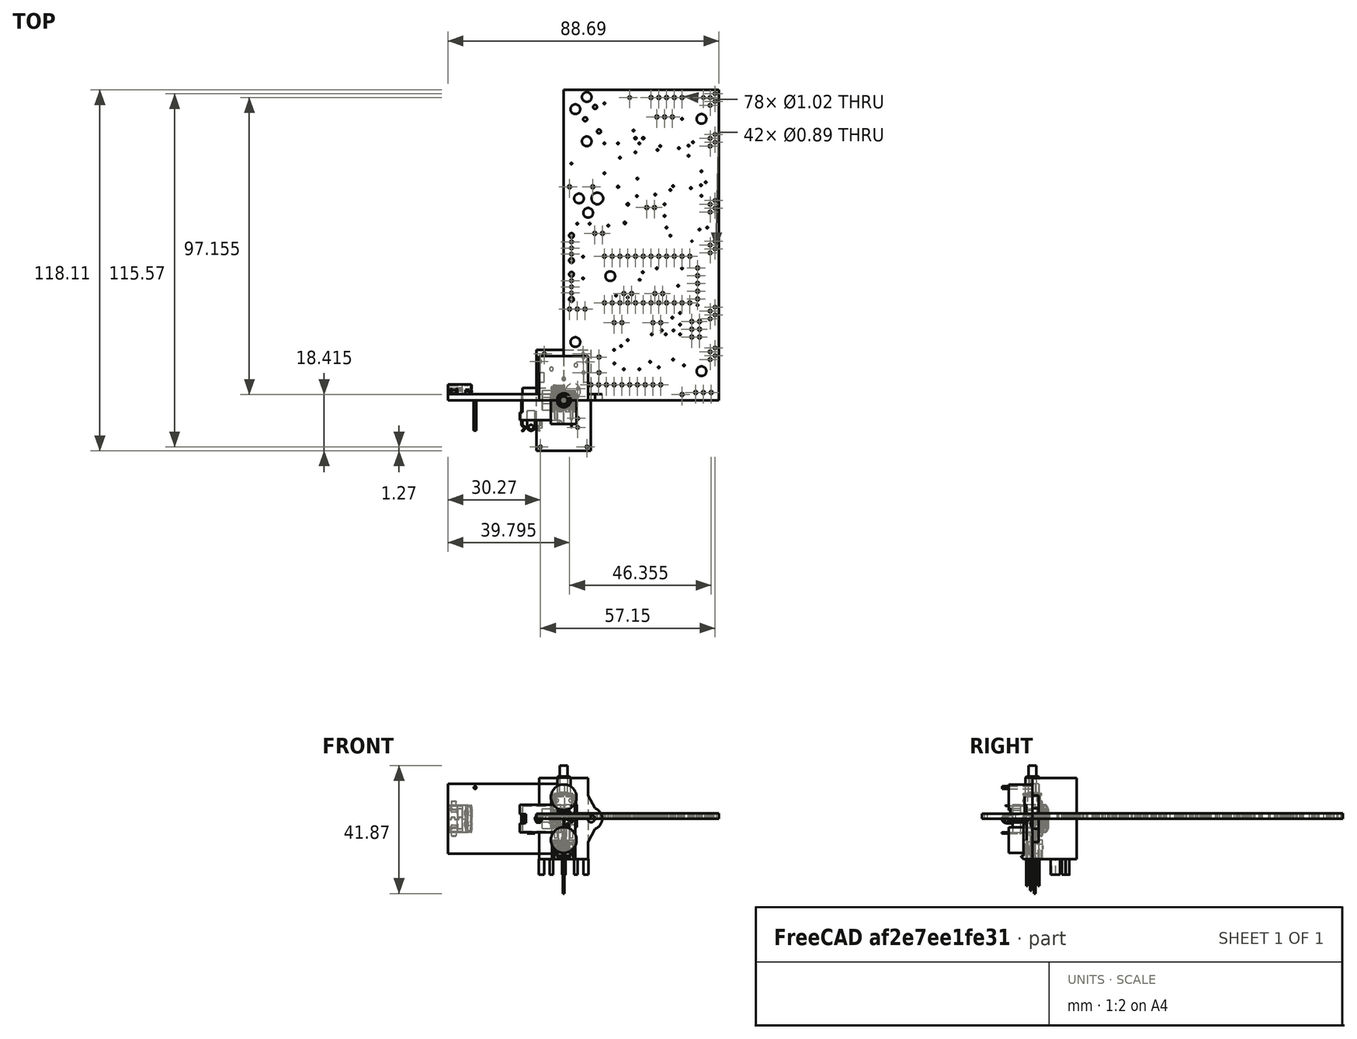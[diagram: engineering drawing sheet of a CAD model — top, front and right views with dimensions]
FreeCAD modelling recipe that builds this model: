
FCSTD DOCUMENT  (FreeCAD 1.0R39109 (Git))
Label: PCB
License: All rights reserved
LicenseURL: https://en.wikipedia.org/wiki/All_rights_reserved
objects: App::Link×17, App::FeaturePython×17, Part::Feature×15, Sketcher::SketchObject×3, App::Part×3, PartDesign::Pad×2, PartDesign::Body×2, PartDesign::Pocket×1, Assembly::JointGroup×1, Assembly::AssemblyObject×1, PartDesign::SubShapeBinder×1
note: 33 computed .brp shape members not serialized (recipe doc carries the construction recipe); baked Part::Feature solids carry a one-line shape summary decoded from their .brp

FEATURE [Sketcher::SketchObject] MainSketch
  ArcFitTolerance = 1e-06
  AttachmentSupport = -> [XY_Plane]
  FullyConstrained = false
  MakeInternals = false
  MapMode = 5
  sketch-geometry (4):
    g0: LineSegment StartX=0 StartY=0 StartZ=0 EndX=50.8 EndY=0 EndZ=0
    g1: LineSegment StartX=50.8 StartY=0 StartZ=0 EndX=50.8 EndY=101.6 EndZ=0
    g2: LineSegment StartX=50.8 StartY=101.6 StartZ=0 EndX=0 EndY=101.6 EndZ=0
    g3: LineSegment StartX=0 StartY=101.6 StartZ=0 EndX=0 EndY=0 EndZ=0
  constraints (4):
    c: Horizontal(g0)
    c: Horizontal(g2)
    c: Vertical(g1)
    c: Vertical(g3)
FEATURE [PartDesign::Pad] Main
  Direction = (0,0,1)
  Length = 1.778
  Length2 = 100.076
  Profile = -> MainSketch
  Refine = true
  Suppressed = false
  Type = 0
FEATURE [Sketcher::SketchObject] HoleSketch
  ArcFitTolerance = 1e-06
  AttachmentSupport = -> [XY_Plane]
  FullyConstrained = false
  MakeInternals = false
  MapMode = 5
  sketch-geometry (197):
    g0: Circle CenterX=41.275 CenterY=47.117 CenterZ=0 NormalX=0 NormalY=0 NormalZ=1 AngleXU=0 Radius=0.508
    g1: Circle CenterX=38.735 CenterY=47.117 CenterZ=0 NormalX=0 NormalY=0 NormalZ=1 AngleXU=0 Radius=0.508
    g2: Circle CenterX=36.195 CenterY=47.117 CenterZ=0 NormalX=0 NormalY=0 NormalZ=1 AngleXU=0 Radius=0.508
    g3: Circle CenterX=13.335 CenterY=47.117 CenterZ=0 NormalX=0 NormalY=0 NormalZ=1 AngleXU=0 Radius=0.508
    g4: Circle CenterX=33.655 CenterY=47.117 CenterZ=0 NormalX=0 NormalY=0 NormalZ=1 AngleXU=0 Radius=0.508
    g5: Circle CenterX=15.875 CenterY=47.117 CenterZ=0 NormalX=0 NormalY=0 NormalZ=1 AngleXU=0 Radius=0.508
    g6: Circle CenterX=31.115 CenterY=47.117 CenterZ=0 NormalX=0 NormalY=0 NormalZ=1 AngleXU=0 Radius=0.508
    g7: Circle CenterX=28.575 CenterY=47.117 CenterZ=0 NormalX=0 NormalY=0 NormalZ=1 AngleXU=0 Radius=0.508
    g8: Circle CenterX=26.035 CenterY=47.117 CenterZ=0 NormalX=0 NormalY=0 NormalZ=1 AngleXU=0 Radius=0.508
    g9: Circle CenterX=18.415 CenterY=47.117 CenterZ=0 NormalX=0 NormalY=0 NormalZ=1 AngleXU=0 Radius=0.508
    g10: Circle CenterX=20.955 CenterY=47.117 CenterZ=0 NormalX=0 NormalY=0 NormalZ=1 AngleXU=0 Radius=0.508
    g11: Circle CenterX=23.495 CenterY=47.117 CenterZ=0 NormalX=0 NormalY=0 NormalZ=1 AngleXU=0 Radius=0.508
    g12: Circle CenterX=15.875 CenterY=31.877 CenterZ=0 NormalX=0 NormalY=0 NormalZ=1 AngleXU=0 Radius=0.508
    g13: Circle CenterX=13.335 CenterY=31.877 CenterZ=0 NormalX=0 NormalY=0 NormalZ=1 AngleXU=0 Radius=0.508
    g14: Circle CenterX=20.955 CenterY=31.877 CenterZ=0 NormalX=0 NormalY=0 NormalZ=1 AngleXU=0 Radius=0.508
    g15: Circle CenterX=18.415 CenterY=31.877 CenterZ=0 NormalX=0 NormalY=0 NormalZ=1 AngleXU=0 Radius=0.508
    g16: Circle CenterX=26.035 CenterY=31.877 CenterZ=0 NormalX=0 NormalY=0 NormalZ=1 AngleXU=0 Radius=0.508
    g17: Circle CenterX=23.495 CenterY=31.877 CenterZ=0 NormalX=0 NormalY=0 NormalZ=1 AngleXU=0 Radius=0.508
    g18: Circle CenterX=31.115 CenterY=31.877 CenterZ=0 NormalX=0 NormalY=0 NormalZ=1 AngleXU=0 Radius=0.508
    g19: Circle CenterX=28.575 CenterY=31.877 CenterZ=0 NormalX=0 NormalY=0 NormalZ=1 AngleXU=0 Radius=0.508
    g20: Circle CenterX=36.195 CenterY=31.877 CenterZ=0 NormalX=0 NormalY=0 NormalZ=1 AngleXU=0 Radius=0.508
    g21: Circle CenterX=33.655 CenterY=31.877 CenterZ=0 NormalX=0 NormalY=0 NormalZ=1 AngleXU=0 Radius=0.508
    g22: Circle CenterX=41.275 CenterY=31.877 CenterZ=0 NormalX=0 NormalY=0 NormalZ=1 AngleXU=0 Radius=0.508
    g23: Circle CenterX=38.735 CenterY=31.877 CenterZ=0 NormalX=0 NormalY=0 NormalZ=1 AngleXU=0 Radius=0.508
    g24: Circle CenterX=22.225 CenterY=34.925 CenterZ=0 NormalX=0 NormalY=0 NormalZ=1 AngleXU=0 Radius=0.508
    g25: Circle CenterX=19.685 CenterY=34.925 CenterZ=0 NormalX=0 NormalY=0 NormalZ=1 AngleXU=0 Radius=0.508
    g26: Circle CenterX=32.385 CenterY=34.925 CenterZ=0 NormalX=0 NormalY=0 NormalZ=1 AngleXU=0 Radius=0.508
    g27: Circle CenterX=29.845 CenterY=34.925 CenterZ=0 NormalX=0 NormalY=0 NormalZ=1 AngleXU=0 Radius=0.508
    g28: Circle CenterX=43.815 CenterY=43.307 CenterZ=0 NormalX=0 NormalY=0 NormalZ=1 AngleXU=0 Radius=0.508
    g29: Circle CenterX=43.815 CenterY=40.767 CenterZ=0 NormalX=0 NormalY=0 NormalZ=1 AngleXU=0 Radius=0.508
    g30: Circle CenterX=43.815 CenterY=38.227 CenterZ=0 NormalX=0 NormalY=0 NormalZ=1 AngleXU=0 Radius=0.508
    g31: Circle CenterX=43.815 CenterY=35.687 CenterZ=0 NormalX=0 NormalY=0 NormalZ=1 AngleXU=0 Radius=0.508
    g32: Circle CenterX=43.815 CenterY=33.147 CenterZ=0 NormalX=0 NormalY=0 NormalZ=1 AngleXU=0 Radius=0.508
    g33: Circle CenterX=16.51 CenterY=25.4 CenterZ=0 NormalX=0 NormalY=0 NormalZ=1 AngleXU=0 Radius=0.508
    g34: Circle CenterX=8.89 CenterY=5.08 CenterZ=0 NormalX=0 NormalY=0 NormalZ=1 AngleXU=0 Radius=0.508
    g35: Circle CenterX=19.05 CenterY=25.4 CenterZ=0 NormalX=0 NormalY=0 NormalZ=1 AngleXU=0 Radius=0.508
    g36: Circle CenterX=11.43 CenterY=5.08 CenterZ=0 NormalX=0 NormalY=0 NormalZ=1 AngleXU=0 Radius=0.508
    g37: Circle CenterX=13.97 CenterY=5.08 CenterZ=0 NormalX=0 NormalY=0 NormalZ=1 AngleXU=0 Radius=0.508
    g38: Circle CenterX=16.51 CenterY=5.08 CenterZ=0 NormalX=0 NormalY=0 NormalZ=1 AngleXU=0 Radius=0.508
    g39: Circle CenterX=19.05 CenterY=5.08 CenterZ=0 NormalX=0 NormalY=0 NormalZ=1 AngleXU=0 Radius=0.508
    g40: Circle CenterX=21.59 CenterY=5.08 CenterZ=0 NormalX=0 NormalY=0 NormalZ=1 AngleXU=0 Radius=0.508
    g41: Circle CenterX=24.13 CenterY=5.08 CenterZ=0 NormalX=0 NormalY=0 NormalZ=1 AngleXU=0 Radius=0.508
    g42: Circle CenterX=26.67 CenterY=5.08 CenterZ=0 NormalX=0 NormalY=0 NormalZ=1 AngleXU=0 Radius=0.508
    g43: Circle CenterX=29.21 CenterY=25.4 CenterZ=0 NormalX=0 NormalY=0 NormalZ=1 AngleXU=0 Radius=0.508
    g44: Circle CenterX=29.21 CenterY=5.08 CenterZ=0 NormalX=0 NormalY=0 NormalZ=1 AngleXU=0 Radius=0.508
    g45: Circle CenterX=31.75 CenterY=25.4 CenterZ=0 NormalX=0 NormalY=0 NormalZ=1 AngleXU=0 Radius=0.508
    g46: Circle CenterX=31.75 CenterY=5.08 CenterZ=0 NormalX=0 NormalY=0 NormalZ=1 AngleXU=0 Radius=0.508
    g47: Circle CenterX=11.5358 CenterY=9.05933 CenterZ=0 NormalX=0 NormalY=0 NormalZ=1 AngleXU=0 Radius=0.508
    g48: Circle CenterX=11.5358 CenterY=14.1393 CenterZ=0 NormalX=0 NormalY=0 NormalZ=1 AngleXU=0 Radius=0.508
    g49: Circle CenterX=6.45583 CenterY=9.05933 CenterZ=0 NormalX=0 NormalY=0 NormalZ=1 AngleXU=0 Radius=0.508
    g50: Circle CenterX=6.45583 CenterY=14.1393 CenterZ=0 NormalX=0 NormalY=0 NormalZ=1 AngleXU=0 Radius=0.508
    g51: Circle CenterX=6.985 CenterY=29.845 CenterZ=0 NormalX=0 NormalY=0 NormalZ=1 AngleXU=0 Radius=0.508
    g52: Circle CenterX=4.445 CenterY=29.845 CenterZ=0 NormalX=0 NormalY=0 NormalZ=1 AngleXU=0 Radius=0.508
    g53: Circle CenterX=1.905 CenterY=29.845 CenterZ=0 NormalX=0 NormalY=0 NormalZ=1 AngleXU=0 Radius=0.508
    g54: Circle CenterX=44.45 CenterY=25.781 CenterZ=0 NormalX=0 NormalY=0 NormalZ=1 AngleXU=0 Radius=0.508
    g55: Circle CenterX=44.45 CenterY=23.241 CenterZ=0 NormalX=0 NormalY=0 NormalZ=1 AngleXU=0 Radius=0.508
    g56: Circle CenterX=44.45 CenterY=20.701 CenterZ=0 NormalX=0 NormalY=0 NormalZ=1 AngleXU=0 Radius=0.508
    g57: Circle CenterX=41.91 CenterY=25.781 CenterZ=0 NormalX=0 NormalY=0 NormalZ=1 AngleXU=0 Radius=0.508
    g58: Circle CenterX=41.91 CenterY=23.241 CenterZ=0 NormalX=0 NormalY=0 NormalZ=1 AngleXU=0 Radius=0.508
    g59: Circle CenterX=41.91 CenterY=20.701 CenterZ=0 NormalX=0 NormalY=0 NormalZ=1 AngleXU=0 Radius=0.508
    g60: Circle CenterX=43.18 CenterY=2.54 CenterZ=0 NormalX=0 NormalY=0 NormalZ=1 AngleXU=0 Radius=0.508
    g61: Circle CenterX=45.72 CenterY=2.54 CenterZ=0 NormalX=0 NormalY=0 NormalZ=1 AngleXU=0 Radius=0.508
    g62: Circle CenterX=48.26 CenterY=2.54 CenterZ=0 NormalX=0 NormalY=0 NormalZ=1 AngleXU=0 Radius=0.508
    g63: Circle CenterX=28.575 CenterY=99.06 CenterZ=0 NormalX=0 NormalY=0 NormalZ=1 AngleXU=0 Radius=0.508
    g64: Circle CenterX=31.115 CenterY=99.06 CenterZ=0 NormalX=0 NormalY=0 NormalZ=1 AngleXU=0 Radius=0.508
    g65: Circle CenterX=38.735 CenterY=99.06 CenterZ=0 NormalX=0 NormalY=0 NormalZ=1 AngleXU=0 Radius=0.508
    g66: Circle CenterX=36.195 CenterY=99.06 CenterZ=0 NormalX=0 NormalY=0 NormalZ=1 AngleXU=0 Radius=0.508
    g67: Circle CenterX=10.16 CenterY=54.61 CenterZ=0 NormalX=0 NormalY=0 NormalZ=1 AngleXU=0 Radius=0.508
    g68: Circle CenterX=12.7 CenterY=54.61 CenterZ=0 NormalX=0 NormalY=0 NormalZ=1 AngleXU=0 Radius=0.508
    g69: Circle CenterX=13.335 CenterY=97.155 CenterZ=0 NormalX=0 NormalY=0 NormalZ=1 AngleXU=0 Radius=0.254
    g70: Circle CenterX=46.5032 CenterY=71.3317 CenterZ=0 NormalX=0 NormalY=0 NormalZ=1 AngleXU=0 Radius=0.254
    g71: Circle CenterX=30.48 CenterY=92.71 CenterZ=0 NormalX=0 NormalY=0 NormalZ=1 AngleXU=0 Radius=0.508
    g72: Circle CenterX=33.02 CenterY=92.71 CenterZ=0 NormalX=0 NormalY=0 NormalZ=1 AngleXU=0 Radius=0.508
    g73: Circle CenterX=35.56 CenterY=92.71 CenterZ=0 NormalX=0 NormalY=0 NormalZ=1 AngleXU=0 Radius=0.508
    g74: Circle CenterX=45.085 CenterY=66.8867 CenterZ=0 NormalX=0 NormalY=0 NormalZ=1 AngleXU=0 Radius=0.254
    g75: Circle CenterX=25.8445 CenterY=41.91 CenterZ=0 NormalX=0 NormalY=0 NormalZ=1 AngleXU=0 Radius=0.254
    g76: Circle CenterX=44.9157 CenterY=70.4003 CenterZ=0 NormalX=0 NormalY=0 NormalZ=1 AngleXU=0 Radius=0.254
    g77: Circle CenterX=41.6348 CenterY=69.4055 CenterZ=0 NormalX=0 NormalY=0 NormalZ=1 AngleXU=0 Radius=0.254
    g78: Circle CenterX=33.655 CenterY=56.515 CenterZ=0 NormalX=0 NormalY=0 NormalZ=1 AngleXU=0 Radius=0.254
    g79: Circle CenterX=34.925 CenterY=53.8903 CenterZ=0 NormalX=0 NormalY=0 NormalZ=1 AngleXU=0 Radius=0.254
    g80: Circle CenterX=17.78 CenterY=84.074 CenterZ=0 NormalX=0 NormalY=0 NormalZ=1 AngleXU=0 Radius=0.254
    g81: Circle CenterX=38.735 CenterY=43.18 CenterZ=0 NormalX=0 NormalY=0 NormalZ=1 AngleXU=0 Radius=0.254
    g82: Circle CenterX=30.48 CenterY=43.18 CenterZ=0 NormalX=0 NormalY=0 NormalZ=1 AngleXU=0 Radius=0.254
    g83: Circle CenterX=24.8708 CenterY=39.4123 CenterZ=0 NormalX=0 NormalY=0 NormalZ=1 AngleXU=0 Radius=0.254
    g84: Circle CenterX=34.925 CenterY=68.7917 CenterZ=0 NormalX=0 NormalY=0 NormalZ=1 AngleXU=0 Radius=0.254
    g85: Circle CenterX=45.72 CenterY=99.06 CenterZ=0 NormalX=0 NormalY=0 NormalZ=1 AngleXU=0 Radius=0.4445
    g86: Circle CenterX=33.02 CenterY=60.325 CenterZ=0 NormalX=0 NormalY=0 NormalZ=1 AngleXU=0 Radius=0.254
    g87: Circle CenterX=38.735 CenterY=1.905 CenterZ=0 NormalX=0 NormalY=0 NormalZ=1 AngleXU=0 Radius=0.508
    g88: Circle CenterX=29.6968 CenterY=63.0555 CenterZ=0 NormalX=0 NormalY=0 NormalZ=1 AngleXU=0 Radius=0.508
    g89: Circle CenterX=27.1568 CenterY=63.0555 CenterZ=0 NormalX=0 NormalY=0 NormalZ=1 AngleXU=0 Radius=0.508
    g90: Circle CenterX=17.78 CenterY=69.85 CenterZ=0 NormalX=0 NormalY=0 NormalZ=1 AngleXU=0 Radius=0.3175
    g91: Circle CenterX=29.9508 CenterY=67.3312 CenterZ=0 NormalX=0 NormalY=0 NormalZ=1 AngleXU=0 Radius=0.254
    g92: Circle CenterX=23.9183 CenterY=66.8232 CenterZ=0 NormalX=0 NormalY=0 NormalZ=1 AngleXU=0 Radius=0.254
    g93: Circle CenterX=4.99533 CenterY=66.04 CenterZ=0 NormalX=0 NormalY=0 NormalZ=1 AngleXU=0 Radius=1.5875
    g94: Circle CenterX=11.0067 CenterY=66.04 CenterZ=0 NormalX=0 NormalY=0 NormalZ=1 AngleXU=0 Radius=1.905
    g95: Circle CenterX=8.001 CenterY=61.341 CenterZ=0 NormalX=0 NormalY=0 NormalZ=1 AngleXU=0 Radius=1.5875
    g96: Circle CenterX=11.5358 CenterY=87.9687 CenterZ=0 NormalX=0 NormalY=0 NormalZ=1 AngleXU=0 Radius=0.656167
    g97: Circle CenterX=10.2764 CenterY=95.9697 CenterZ=0 NormalX=0 NormalY=0 NormalZ=1 AngleXU=0 Radius=0.661458
    g98: Circle CenterX=7.02733 CenterY=91.9692 CenterZ=0 NormalX=0 NormalY=0 NormalZ=1 AngleXU=0 Radius=0.656167
    g99: Circle CenterX=7.53533 CenterY=84.7302 CenterZ=0 NormalX=0 NormalY=0 NormalZ=1 AngleXU=0 Radius=1.5875
    g100: Circle CenterX=7.53533 CenterY=99.2293 CenterZ=0 NormalX=0 NormalY=0 NormalZ=1 AngleXU=0 Radius=1.5875
    g101: Circle CenterX=13.335 CenterY=84.0528 CenterZ=0 NormalX=0 NormalY=0 NormalZ=1 AngleXU=0 Radius=0.254
    g102: Circle CenterX=33.02 CenterY=64.135 CenterZ=0 NormalX=0 NormalY=0 NormalZ=1 AngleXU=0 Radius=0.254
    g103: Circle CenterX=17.145 CenterY=34.29 CenterZ=0 NormalX=0 NormalY=0 NormalZ=1 AngleXU=0 Radius=0.254
    g104: Circle CenterX=38.1 CenterY=21.59 CenterZ=0 NormalX=0 NormalY=0 NormalZ=1 AngleXU=0 Radius=0.254
    g105: Circle CenterX=35.56 CenterY=27.0722 CenterZ=0 NormalX=0 NormalY=0 NormalZ=1 AngleXU=0 Radius=0.254
    g106: Circle CenterX=38.1 CenterY=24.765 CenterZ=0 NormalX=0 NormalY=0 NormalZ=1 AngleXU=0 Radius=0.254
    g107: Circle CenterX=38.1 CenterY=28.575 CenterZ=0 NormalX=0 NormalY=0 NormalZ=1 AngleXU=0 Radius=0.254
    g108: Circle CenterX=20.955 CenterY=33.655 CenterZ=0 NormalX=0 NormalY=0 NormalZ=1 AngleXU=0 Radius=0.254
    g109: Circle CenterX=43.815 CenterY=31.115 CenterZ=0 NormalX=0 NormalY=0 NormalZ=1 AngleXU=0 Radius=0.254
    g110: Circle CenterX=45.085 CenterY=9.525 CenterZ=0 NormalX=0 NormalY=0 NormalZ=1 AngleXU=0 Radius=1.5875
    g111: Circle CenterX=45.085 CenterY=92.075 CenterZ=0 NormalX=0 NormalY=0 NormalZ=1 AngleXU=0 Radius=1.5875
    g112: Circle CenterX=35.814 CenterY=70.0617 CenterZ=0 NormalX=0 NormalY=0 NormalZ=1 AngleXU=0 Radius=0.254
    g113: Circle CenterX=3.81 CenterY=95.25 CenterZ=0 NormalX=0 NormalY=0 NormalZ=1 AngleXU=0 Radius=1.5875
    g114: Circle CenterX=37.465 CenterY=37.465 CenterZ=0 NormalX=0 NormalY=0 NormalZ=1 AngleXU=0 Radius=0.254
    g115: Circle CenterX=21.59 CenterY=99.06 CenterZ=0 NormalX=0 NormalY=0 NormalZ=1 AngleXU=0 Radius=0.4445
    g116: Circle CenterX=35.814 CenterY=13.335 CenterZ=0 NormalX=0 NormalY=0 NormalZ=1 AngleXU=0 Radius=0.254
    g117: Circle CenterX=28.829 CenterY=21.59 CenterZ=0 NormalX=0 NormalY=0 NormalZ=1 AngleXU=0 Radius=0.254
    g118: Circle CenterX=33.401 CenterY=21.59 CenterZ=0 NormalX=0 NormalY=0 NormalZ=1 AngleXU=0 Radius=0.254
    g119: Circle CenterX=35.941 CenterY=22.86 CenterZ=0 NormalX=0 NormalY=0 NormalZ=1 AngleXU=0 Radius=0.254
    g120: Circle CenterX=32.131 CenterY=22.86 CenterZ=0 NormalX=0 NormalY=0 NormalZ=1 AngleXU=0 Radius=0.254
    g121: Circle CenterX=18.796 CenterY=17.7377 CenterZ=0 NormalX=0 NormalY=0 NormalZ=1 AngleXU=0 Radius=0.254
    g122: Circle CenterX=28.2575 CenterY=12.5942 CenterZ=0 NormalX=0 NormalY=0 NormalZ=1 AngleXU=0 Radius=0.254
    g123: Circle CenterX=20.955 CenterY=19.685 CenterZ=0 NormalX=0 NormalY=0 NormalZ=1 AngleXU=0 Radius=0.254
    g124: Circle CenterX=24.765 CenterY=10.16 CenterZ=0 NormalX=0 NormalY=0 NormalZ=1 AngleXU=0 Radius=0.254
    g125: Circle CenterX=16.5523 CenterY=12.065 CenterZ=0 NormalX=0 NormalY=0 NormalZ=1 AngleXU=0 Radius=0.254
    g126: Circle CenterX=16.4888 CenterY=16.51 CenterZ=0 NormalX=0 NormalY=0 NormalZ=1 AngleXU=0 Radius=0.254
    g127: Circle CenterX=19.685 CenterY=10.16 CenterZ=0 NormalX=0 NormalY=0 NormalZ=1 AngleXU=0 Radius=0.254
    g128: Circle CenterX=39.37 CenterY=11.43 CenterZ=0 NormalX=0 NormalY=0 NormalZ=1 AngleXU=0 Radius=0.254
    g129: Circle CenterX=33.655 CenterY=99.06 CenterZ=0 NormalX=0 NormalY=0 NormalZ=1 AngleXU=0 Radius=0.508
    g130: Circle CenterX=3.81 CenterY=19.05 CenterZ=0 NormalX=0 NormalY=0 NormalZ=1 AngleXU=0 Radius=1.5875
    g131: Circle CenterX=15.24 CenterY=40.6188 CenterZ=0 NormalX=0 NormalY=0 NormalZ=1 AngleXU=0 Radius=1.5875
    g132: Circle CenterX=42.3122 CenterY=84.455 CenterZ=0 NormalX=0 NormalY=0 NormalZ=1 AngleXU=0 Radius=0.254
    g133: Circle CenterX=40.8517 CenterY=80.01 CenterZ=0 NormalX=0 NormalY=0 NormalZ=1 AngleXU=0 Radius=0.254
    g134: Circle CenterX=40.8517 CenterY=83.3332 CenterZ=0 NormalX=0 NormalY=0 NormalZ=1 AngleXU=0 Radius=0.254
    g135: Circle CenterX=37.6767 CenterY=82.4865 CenterZ=0 NormalX=0 NormalY=0 NormalZ=1 AngleXU=0 Radius=0.254
    g136: Circle CenterX=30.6917 CenterY=81.915 CenterZ=0 NormalX=0 NormalY=0 NormalZ=1 AngleXU=0 Radius=0.254
    g137: Circle CenterX=31.5807 CenterY=83.185 CenterZ=0 NormalX=0 NormalY=0 NormalZ=1 AngleXU=0 Radius=0.254
    g138: Circle CenterX=38.735 CenterY=92.075 CenterZ=0 NormalX=0 NormalY=0 NormalZ=1 AngleXU=0 Radius=0.254
    g139: Circle CenterX=3.048 CenterY=3.048 CenterZ=0 NormalX=0 NormalY=0 NormalZ=1 AngleXU=0 Radius=2.43417
    g140: Circle CenterX=2.54 CenterY=77.47 CenterZ=0 NormalX=0 NormalY=0 NormalZ=1 AngleXU=0 Radius=0.254
    g141: Circle CenterX=26.0244 CenterY=85.7673 CenterZ=0 NormalX=0 NormalY=0 NormalZ=1 AngleXU=0 Radius=0.365125
    g142: Circle CenterX=23.4844 CenterY=85.7673 CenterZ=0 NormalX=0 NormalY=0 NormalZ=1 AngleXU=0 Radius=0.365125
    g143: Circle CenterX=24.765 CenterY=84.0317 CenterZ=0 NormalX=0 NormalY=0 NormalZ=1 AngleXU=0 Radius=0.254
    g144: Circle CenterX=18.415 CenterY=79.375 CenterZ=0 NormalX=0 NormalY=0 NormalZ=1 AngleXU=0 Radius=0.254
    g145: Circle CenterX=23.495 CenterY=81.1318 CenterZ=0 NormalX=0 NormalY=0 NormalZ=1 AngleXU=0 Radius=0.254
    g146: Circle CenterX=2.56117 CenterY=51.8372 CenterZ=0 NormalX=0 NormalY=0 NormalZ=1 AngleXU=0 Radius=0.4445
    g147: Circle CenterX=2.56117 CenterY=47.8367 CenterZ=0 NormalX=0 NormalY=0 NormalZ=1 AngleXU=0 Radius=0.4445
    g148: Circle CenterX=2.55058 CenterY=45.7306 CenterZ=0 NormalX=0 NormalY=0 NormalZ=1 AngleXU=0 Radius=0.772583
    g149: Circle CenterX=2.55058 CenterY=53.9221 CenterZ=0 NormalX=0 NormalY=0 NormalZ=1 AngleXU=0 Radius=0.772583
    g150: Circle CenterX=2.56117 CenterY=49.8263 CenterZ=0 NormalX=0 NormalY=0 NormalZ=1 AngleXU=0 Radius=0.4445
    g151: Circle CenterX=2.56117 CenterY=39.1372 CenterZ=0 NormalX=0 NormalY=0 NormalZ=1 AngleXU=0 Radius=0.4445
    g152: Circle CenterX=2.56117 CenterY=35.1367 CenterZ=0 NormalX=0 NormalY=0 NormalZ=1 AngleXU=0 Radius=0.4445
    g153: Circle CenterX=2.55058 CenterY=33.0306 CenterZ=0 NormalX=0 NormalY=0 NormalZ=1 AngleXU=0 Radius=0.772583
    g154: Circle CenterX=2.55058 CenterY=41.2327 CenterZ=0 NormalX=0 NormalY=0 NormalZ=1 AngleXU=0 Radius=0.777875
    g155: Circle CenterX=2.56117 CenterY=37.1263 CenterZ=0 NormalX=0 NormalY=0 NormalZ=1 AngleXU=0 Radius=0.4445
    g156: Circle CenterX=22.86 CenterY=88.265 CenterZ=0 NormalX=0 NormalY=0 NormalZ=1 AngleXU=0 Radius=0.254
    g157: Circle CenterX=6.35 CenterY=39.9203 CenterZ=0 NormalX=0 NormalY=0 NormalZ=1 AngleXU=0 Radius=0.254
    g158: Circle CenterX=31.115 CenterY=10.795 CenterZ=0 NormalX=0 NormalY=0 NormalZ=1 AngleXU=0 Radius=0.254
    g159: Circle CenterX=20.0025 CenterY=58.0496 CenterZ=0 NormalX=0 NormalY=0 NormalZ=1 AngleXU=0 Radius=0.365125
    g160: Circle CenterX=4.445 CenterY=57.785 CenterZ=0 NormalX=0 NormalY=0 NormalZ=1 AngleXU=0 Radius=0.254
    g161: Circle CenterX=6.35 CenterY=46.99 CenterZ=0 NormalX=0 NormalY=0 NormalZ=1 AngleXU=0 Radius=0.254
    g162: Circle CenterX=8.509 CenterY=57.8062 CenterZ=0 NormalX=0 NormalY=0 NormalZ=1 AngleXU=0 Radius=0.254
    g163: Circle CenterX=14.605 CenterY=57.15 CenterZ=0 NormalX=0 NormalY=0 NormalZ=1 AngleXU=0 Radius=0.254
    g164: Circle CenterX=24.13 CenterY=72.5593 CenterZ=0 NormalX=0 NormalY=0 NormalZ=1 AngleXU=0 Radius=0.254
    g165: Circle CenterX=13.335 CenterY=74.295 CenterZ=0 NormalX=0 NormalY=0 NormalZ=1 AngleXU=0 Radius=0.254
    g166: Circle CenterX=20.9444 CenterY=64.1244 CenterZ=0 NormalX=0 NormalY=0 NormalZ=1 AngleXU=0 Radius=0.370417
    g167: Circle CenterX=9.525 CenterY=69.85 CenterZ=0 NormalX=0 NormalY=0 NormalZ=1 AngleXU=0 Radius=0.508
    g168: Circle CenterX=1.905 CenterY=69.85 CenterZ=0 NormalX=0 NormalY=0 NormalZ=1 AngleXU=0 Radius=0.508
    g169: Circle CenterX=49.53 CenterY=100.33 CenterZ=0 NormalX=0 NormalY=0 NormalZ=1 AngleXU=0 Radius=0.4445
    g170: Circle CenterX=47.9213 CenterY=99.06 CenterZ=0 NormalX=0 NormalY=0 NormalZ=1 AngleXU=0 Radius=0.4445
    g171: Circle CenterX=49.53 CenterY=97.79 CenterZ=0 NormalX=0 NormalY=0 NormalZ=1 AngleXU=0 Radius=0.4445
    g172: Circle CenterX=47.9213 CenterY=96.52 CenterZ=0 NormalX=0 NormalY=0 NormalZ=1 AngleXU=0 Radius=0.4445
    g173: Circle CenterX=49.53 CenterY=86.995 CenterZ=0 NormalX=0 NormalY=0 NormalZ=1 AngleXU=0 Radius=0.4445
    g174: Circle CenterX=47.9213 CenterY=85.725 CenterZ=0 NormalX=0 NormalY=0 NormalZ=1 AngleXU=0 Radius=0.4445
    g175: Circle CenterX=49.53 CenterY=84.455 CenterZ=0 NormalX=0 NormalY=0 NormalZ=1 AngleXU=0 Radius=0.4445
    g176: Circle CenterX=47.9213 CenterY=83.185 CenterZ=0 NormalX=0 NormalY=0 NormalZ=1 AngleXU=0 Radius=0.4445
    g177: Circle CenterX=49.53 CenterY=65.405 CenterZ=0 NormalX=0 NormalY=0 NormalZ=1 AngleXU=0 Radius=0.4445
    g178: Circle CenterX=47.9213 CenterY=64.135 CenterZ=0 NormalX=0 NormalY=0 NormalZ=1 AngleXU=0 Radius=0.4445
    g179: Circle CenterX=49.53 CenterY=62.865 CenterZ=0 NormalX=0 NormalY=0 NormalZ=1 AngleXU=0 Radius=0.4445
    g180: Circle CenterX=47.9213 CenterY=61.595 CenterZ=0 NormalX=0 NormalY=0 NormalZ=1 AngleXU=0 Radius=0.4445
    g181: Circle CenterX=49.53 CenterY=52.07 CenterZ=0 NormalX=0 NormalY=0 NormalZ=1 AngleXU=0 Radius=0.4445
    g182: Circle CenterX=47.9213 CenterY=50.8 CenterZ=0 NormalX=0 NormalY=0 NormalZ=1 AngleXU=0 Radius=0.4445
    g183: Circle CenterX=49.53 CenterY=49.53 CenterZ=0 NormalX=0 NormalY=0 NormalZ=1 AngleXU=0 Radius=0.4445
    g184: Circle CenterX=47.9213 CenterY=48.26 CenterZ=0 NormalX=0 NormalY=0 NormalZ=1 AngleXU=0 Radius=0.4445
    g185: Circle CenterX=49.53 CenterY=30.48 CenterZ=0 NormalX=0 NormalY=0 NormalZ=1 AngleXU=0 Radius=0.4445
    g186: Circle CenterX=47.9213 CenterY=29.21 CenterZ=0 NormalX=0 NormalY=0 NormalZ=1 AngleXU=0 Radius=0.4445
    g187: Circle CenterX=49.53 CenterY=27.94 CenterZ=0 NormalX=0 NormalY=0 NormalZ=1 AngleXU=0 Radius=0.4445
    g188: Circle CenterX=47.9213 CenterY=26.67 CenterZ=0 NormalX=0 NormalY=0 NormalZ=1 AngleXU=0 Radius=0.4445
    g189: Circle CenterX=49.53 CenterY=17.145 CenterZ=0 NormalX=0 NormalY=0 NormalZ=1 AngleXU=0 Radius=0.4445
    g190: Circle CenterX=47.9213 CenterY=15.875 CenterZ=0 NormalX=0 NormalY=0 NormalZ=1 AngleXU=0 Radius=0.4445
    g191: Circle CenterX=49.53 CenterY=14.605 CenterZ=0 NormalX=0 NormalY=0 NormalZ=1 AngleXU=0 Radius=0.4445
    g192: Circle CenterX=47.9213 CenterY=13.335 CenterZ=0 NormalX=0 NormalY=0 NormalZ=1 AngleXU=0 Radius=0.4445
    g193: Circle CenterX=45.085 CenterY=74.93 CenterZ=0 NormalX=0 NormalY=0 NormalZ=1 AngleXU=0 Radius=0.254
    g194: Circle CenterX=46.99 CenterY=56.515 CenterZ=0 NormalX=0 NormalY=0 NormalZ=1 AngleXU=0 Radius=0.254
    g195: Circle CenterX=44.45 CenterY=55.88 CenterZ=0 NormalX=0 NormalY=0 NormalZ=1 AngleXU=0 Radius=0.254
    g196: Circle CenterX=41.9206 CenterY=52.07 CenterZ=0 NormalX=0 NormalY=0 NormalZ=1 AngleXU=0 Radius=0.174625
FEATURE [PartDesign::Pocket] Holes
  BaseFeature = -> Main
  Direction = (0,0,-1)
  Length = 3.556
  Length2 = 5
  Profile = -> HoleSketch
  Refine = true
  Reversed = true
  Suppressed = false
  Type = 0
FEATURE [PartDesign::Body] Body  label="pcb imported"
  AllowCompound = false
  Group = -> [MainSketch,Main,HoleSketch,Holes]
  Origin = -> Origin
  Tip = -> Holes
FEATURE [App::Link] pcb_imported  label="pcb imported001"
  LinkedObject = -> Body
FEATURE [App::FeaturePython] GroundedJoint  # Assembly grounded joint (typed FeaturePython)
  ObjectToGround = -> pcb_imported
FEATURE [Part::Feature] Part__Feature  label="WP154A4SUREQBFZGC"
  shape: bbox 5.9 x 5.487 x 33.1 mm, 95 faces (baked)
FEATURE [App::Link] WP154A4SUREQBFZGC  label="WP154A4SUREQBFZGC001"
  LinkPlacement = pos=(54.356,15.113,4.572) rot=(0,1,0;1.5708rad)
  LinkedObject = -> Part__Feature
  Placement = pos=(54.356,15.113,4.572) rot=(0,1,0;1.5708rad)
FEATURE [App::FeaturePython] Joint  label="Fixed"  # Assembly joint (typed FeaturePython)
  Activated = true
  AngleMax = 0
  AngleMin = 0
  Detach1 = false
  Detach2 = false
  Distance = 0
  Distance2 = 0
  EnableAngleMax = false
  EnableAngleMin = false
  EnableLengthMax = false
  EnableLengthMin = false
  JointType = 0 (Fixed)
  LengthMax = 0
  LengthMin = 0
  Offset1 = pos=(4.572,-15.113,-54.356) rot=(0.707107,0,0.707107;3.14159rad)
  Placement1 = pos=(4.572,-15.113,-54.356) rot=(0.707107,0,0.707107;3.14159rad)
  Reference1 = -> Assembly [WP154A4SUREQBFZGC.,WP154A4SUREQBFZGC.]
  Reference2 = -> Assembly [pcb_imported.,pcb_imported.]
FEATURE [App::Link] WP154A4SUREQBFZGC001  label="WP154A4SUREQBFZGC002"
  LinkPlacement = pos=(54.356,28.448,4.572) rot=(0,1,0;1.5708rad)
  LinkedObject = -> Part__Feature
  Placement = pos=(54.356,28.448,4.572) rot=(0,1,0;1.5708rad)
FEATURE [App::FeaturePython] Joint001  label="Fixed001"  # Assembly joint (typed FeaturePython)
  Activated = true
  AngleMax = 0
  AngleMin = 0
  Detach1 = false
  Detach2 = false
  Distance = 0
  Distance2 = 0
  EnableAngleMax = false
  EnableAngleMin = false
  EnableLengthMax = false
  EnableLengthMin = false
  JointType = 0 (Fixed)
  LengthMax = 0
  LengthMin = 0
  Offset1 = pos=(0,-13.335,0) rot=(1,0,0;3.14159rad)
  Placement1 = pos=(0,-13.335,0) rot=(1,0,0;3.14159rad)
  Reference1 = -> Assembly [WP154A4SUREQBFZGC001.,WP154A4SUREQBFZGC001.]
  Reference2 = -> Assembly [WP154A4SUREQBFZGC.,WP154A4SUREQBFZGC.]
FEATURE [App::Link] WP154A4SUREQBFZGC002  label="WP154A4SUREQBFZGC003"
  LinkPlacement = pos=(54.356,50.038,4.572) rot=(0,1,0;1.5708rad)
  LinkedObject = -> Part__Feature
  Placement = pos=(54.356,50.038,4.572) rot=(0,1,0;1.5708rad)
FEATURE [App::FeaturePython] Joint002  label="Fixed002"  # Assembly joint (typed FeaturePython)
  Activated = true
  AngleMax = 0
  AngleMin = 0
  Detach1 = false
  Detach2 = false
  Distance = 0
  Distance2 = 0
  EnableAngleMax = false
  EnableAngleMin = false
  EnableLengthMax = false
  EnableLengthMin = false
  JointType = 0 (Fixed)
  LengthMax = 0
  LengthMin = 0
  Offset1 = pos=(0,-34.925,0) rot=(0,0,1;0rad)
  Placement1 = pos=(0,-34.925,0) rot=(0,0,1;0rad)
  Reference1 = -> Assembly [WP154A4SUREQBFZGC002.,WP154A4SUREQBFZGC002.]
  Reference2 = -> Assembly [WP154A4SUREQBFZGC.,WP154A4SUREQBFZGC.]
FEATURE [App::Link] WP154A4SUREQBFZGC003  label="WP154A4SUREQBFZGC004"
  LinkPlacement = pos=(54.356,63.373,4.572) rot=(0,1,0;1.5708rad)
  LinkedObject = -> Part__Feature
  Placement = pos=(54.356,63.373,4.572) rot=(0,1,0;1.5708rad)
FEATURE [App::FeaturePython] Joint003  label="Fixed003"  # Assembly joint (typed FeaturePython)
  Activated = true
  AngleMax = 0
  AngleMin = 0
  Detach1 = false
  Detach2 = false
  Distance = 0
  Distance2 = 0
  EnableAngleMax = false
  EnableAngleMin = false
  EnableLengthMax = false
  EnableLengthMin = false
  JointType = 0 (Fixed)
  LengthMax = 0
  LengthMin = 0
  Offset1 = pos=(0,-13.335,0) rot=(0,0,1;0rad)
  Placement1 = pos=(0,-13.335,0) rot=(0,0,1;0rad)
  Reference1 = -> Assembly [WP154A4SUREQBFZGC003.,WP154A4SUREQBFZGC003.]
  Reference2 = -> Assembly [WP154A4SUREQBFZGC002.,WP154A4SUREQBFZGC002.]
FEATURE [App::Link] WP154A4SUREQBFZGC004  label="WP154A4SUREQBFZGC005"
  LinkPlacement = pos=(54.356,84.963,4.572) rot=(0,1,0;1.5708rad)
  LinkedObject = -> Part__Feature
  Placement = pos=(54.356,84.963,4.572) rot=(0,1,0;1.5708rad)
FEATURE [App::FeaturePython] Joint004  label="Fixed004"  # Assembly joint (typed FeaturePython)
  Activated = true
  AngleMax = 0
  AngleMin = 0
  Detach1 = false
  Detach2 = false
  Distance = 0
  Distance2 = 0
  EnableAngleMax = false
  EnableAngleMin = false
  EnableLengthMax = false
  EnableLengthMin = false
  JointType = 0 (Fixed)
  LengthMax = 0
  LengthMin = 0
  Offset1 = pos=(0,34.925,0) rot=(0,0,1;0rad)
  Placement1 = pos=(0,34.925,0) rot=(0,0,1;0rad)
  Reference1 = -> Assembly [WP154A4SUREQBFZGC002.,WP154A4SUREQBFZGC002.]
  Reference2 = -> Assembly [WP154A4SUREQBFZGC004.,WP154A4SUREQBFZGC004.]
FEATURE [App::Link] WP154A4SUREQBFZGC005  label="WP154A4SUREQBFZGC006"
  LinkPlacement = pos=(54.356,98.298,4.572) rot=(0,1,0;1.5708rad)
  LinkedObject = -> Part__Feature
  Placement = pos=(54.356,98.298,4.572) rot=(0,1,0;1.5708rad)
FEATURE [App::FeaturePython] Joint005  label="Fixed005"  # Assembly joint (typed FeaturePython)
  Activated = true
  AngleMax = 0
  AngleMin = 0
  Detach1 = false
  Detach2 = false
  Distance = 0
  Distance2 = 0
  EnableAngleMax = false
  EnableAngleMin = false
  EnableLengthMax = false
  EnableLengthMin = false
  JointType = 0 (Fixed)
  LengthMax = 0
  LengthMin = 0
  Offset1 = pos=(0,-13.335,0) rot=(0,0,1;0rad)
  Placement1 = pos=(0,-13.335,0) rot=(0,0,1;0rad)
  Reference1 = -> Assembly [WP154A4SUREQBFZGC005.,WP154A4SUREQBFZGC005.]
  Reference2 = -> Assembly [WP154A4SUREQBFZGC004.,WP154A4SUREQBFZGC004.]
FEATURE [Part::Feature] Part__Feature003  label="Dual RCA"
  shape: bbox 20.7 x 22.3 x 31.6 mm, 33 faces (baked)
FEATURE [App::Link] Dual_RCA  label="Dual RCA001"
  LinkPlacement = pos=(0.032625,91.9586,15.028) rot=(0,0,-1;1.5708rad)
  LinkedObject = -> Part__Feature003
  Placement = pos=(0.032625,91.9586,15.028) rot=(0,0,-1;1.5708rad)
FEATURE [App::FeaturePython] Joint008  label="Fixed008"  # Assembly joint (typed FeaturePython)
  Activated = true
  AngleMax = 0
  AngleMin = 0
  Detach1 = false
  Detach2 = false
  Distance = 0
  Distance2 = 0
  EnableAngleMax = false
  EnableAngleMin = false
  EnableLengthMax = false
  EnableLengthMin = false
  JointType = 0 (Fixed)
  LengthMax = 0
  LengthMin = 0
  Offset1 = pos=(-13.335,33.909,0) rot=(0,0,1;1.5708rad)
  Placement1 = pos=(7.03262,91.9586,1.778) rot=(0,0,1;1.5708rad)
  Placement2 = pos=(-1.42e-14,7,-13.25) rot=(0,1,0;3.14159rad)
  Reference1 = -> Assembly [pcb_imported.Face5,pcb_imported.Vertex332]
  Reference2 = -> Assembly [Dual_RCA.Face1,Dual_RCA.Edge1]
FEATURE [Part::Feature] Part__Feature004  label="Pro Mini"
  shape: bbox 17.78 x 33.02 x 1.588 mm, 16 faces (baked)
FEATURE [App::Link] Pro_Mini  label="Pro Mini001"
  LinkPlacement = pos=(28.575,39.37,11.938) rot=(0,0,1;4.71239rad)
  LinkedObject = -> Part__Feature004
  Placement = pos=(28.575,39.37,11.938) rot=(0,0,1;4.71239rad)
FEATURE [App::FeaturePython] Joint009  label="Fixed009"  # Assembly joint (typed FeaturePython)
  Activated = true
  AngleMax = 0
  AngleMin = 0
  Detach1 = false
  Detach2 = false
  Distance = 0
  Distance2 = 0
  EnableAngleMax = false
  EnableAngleMin = false
  EnableLengthMax = false
  EnableLengthMin = false
  JointType = 0 (Fixed)
  LengthMax = 0
  LengthMin = 0
  Offset1 = pos=(39.37,-28.575,-11.938) rot=(0,0,1;1.5708rad)
  Placement1 = pos=(39.37,-28.575,-11.938) rot=(0,0,1;1.5708rad)
  Reference1 = -> Assembly [Pro_Mini.,Pro_Mini.]
  Reference2 = -> Assembly [pcb_imported.,pcb_imported.]
FEATURE [Part::Feature] Part__Feature005  label="Body1"
  shape: bbox 8.13 x 5.08 x 8.03 mm, 51 faces (baked)
FEATURE [Part::Feature] Part__Feature006  label="Body2"
  shape: bbox 8.13 x 5.08 x 6.63 mm, 28 faces (baked)
FEATURE [Part::Feature] Part__Feature007  label="Body3"
  shape: bbox 8.13 x 8.61 x 1.39 mm, 44 faces (baked)
FEATURE [Part::Feature] Part__Feature008  label="Body4"
  shape: bbox 6.101 x 6.101 x 6.101 mm, 9 faces (baked)
FEATURE [Part::Feature] Part__Feature009  label="Body5"
  shape: bbox 8 x 11.33 x 3.705 mm, 42 faces (baked)
FEATURE [Part::Feature] Part__Feature010  label="Body6"
  shape: bbox 2.54 x 2.54 x 6 mm, 3 faces (baked)
FEATURE [App::Part] _00SP9B6M6RE__3DModel_STEP_520916  label="800SP9B6M6RE--3DModel-STEP-520916"
  Group = -> [Part__Feature005,Part__Feature006,Part__Feature007,Part__Feature008,Part__Feature009,Part__Feature010]
  Origin = -> Origin002
  Placement = pos=(0,3.05,-1.7005) rot=(0,0,1;0rad)
FEATURE [App::Part] SPST_momentary  label="SPST-momentary"
  Group = -> [_00SP9B6M6RE__3DModel_STEP_520916]
  Origin = -> Origin003
FEATURE [App::Link] SPST_momentary001  label="SPST-momentary001"
  LinkPlacement = pos=(9.02102,11.6417,1.678) rot=(-0.57735,0.57735,0.57735;4.18879rad)
  LinkedObject = -> SPST_momentary
  Placement = pos=(9.02102,11.6417,1.678) rot=(-0.57735,0.57735,0.57735;4.18879rad)
FEATURE [App::FeaturePython] Joint010  label="Fixed010"  # Assembly joint (typed FeaturePython)
  Activated = true
  AngleMax = 0
  AngleMin = 0
  Detach1 = false
  Detach2 = false
  Distance = 0
  Distance2 = 0
  EnableAngleMax = false
  EnableAngleMin = false
  EnableLengthMax = false
  EnableLengthMin = false
  JointType = 0 (Fixed)
  LengthMax = 0
  LengthMin = 0
  Offset1 = pos=(-14.224,-6.096,0) rot=(0,0,1;3.14159rad)
  Placement1 = pos=(4.826,11.6417,1.778) rot=(0,0,1;3.14159rad)
  Placement2 = pos=(2e-16,-2.95,5.89552) rot=(0.57735,0.57735,0.57735;4.18879rad)
  Reference1 = -> Assembly [pcb_imported.Face5,pcb_imported.Vertex223]
  Reference2 = -> Assembly [SPST_momentary001._00SP9B6M6RE__3DModel_STEP_520916.Part__Feature009.Face24,SPST_momentary001._00SP9B6M6RE__3DModel_STEP_520916.Part__Feature009.Face24]
FEATURE [Part::Feature] Part__Feature011  label="3pinconnector-640441-3"
  shape: bbox 7.62 x 7.087 x 13.21 mm, 307 faces (baked)
FEATURE [App::Link] _pinconnector_640441_3  label="3pinconnector-640441-004"
  LinkPlacement = pos=(45.7412,2.54,1.778) rot=(0,1,0;3.14159rad)
  LinkedObject = -> Part__Feature011
  Placement = pos=(45.7412,2.54,1.778) rot=(0,1,0;3.14159rad)
FEATURE [App::FeaturePython] Joint011  label="Fixed011"  # Assembly joint (typed FeaturePython)
  Activated = true
  AngleMax = 0
  AngleMin = 0
  Detach1 = false
  Detach2 = false
  Distance = 0
  Distance2 = 0
  EnableAngleMax = false
  EnableAngleMin = false
  EnableLengthMax = false
  EnableLengthMin = false
  JointType = 0 (Fixed)
  LengthMax = 0
  LengthMin = 0
  Offset1 = pos=(41.148,1.27,0) rot=(0,0,1;3.14159rad)
  Placement1 = pos=(40.259,0.508,2e-16) rot=(0,0,1;3.14159rad)
  Placement2 = pos=(5.48217,3.048,1.778) rot=(0,0,1;0rad)
  Reference1 = -> Assembly [_pinconnector_640441_3.Face186,_pinconnector_640441_3.Vertex340]
  Reference2 = -> Assembly [pcb_imported.Face5,pcb_imported.Vertex206]
FEATURE [App::Link] _pinconnector_640441_004  label="3pinconnector-640441-005"
  LinkPlacement = pos=(4.445,29.845,1.778) rot=(0,1,0;3.14159rad)
  LinkedObject = -> Part__Feature011
  Placement = pos=(4.445,29.845,1.778) rot=(0,1,0;3.14159rad)
FEATURE [App::FeaturePython] Joint012  label="Fixed012"  # Assembly joint (typed FeaturePython)
  Activated = true
  AngleMax = 0
  AngleMin = 0
  Detach1 = false
  Detach2 = false
  Distance = 0
  Distance2 = 0
  EnableAngleMax = false
  EnableAngleMin = false
  EnableLengthMax = false
  EnableLengthMin = false
  JointType = 0 (Fixed)
  LengthMax = 0
  LengthMin = 0
  Offset1 = pos=(-23.749,-2.794,0) rot=(0,0,1;3.14159rad)
  Placement1 = pos=(2.794,29.083,1.778) rot=(0,0,1;3.14159rad)
  Placement2 = pos=(1.651,-0.762,2e-16) rot=(0,0,1;0rad)
  Reference1 = -> Assembly [pcb_imported.Face5,pcb_imported.Vertex284]
  Reference2 = -> Assembly [_pinconnector_640441_004.Face186,_pinconnector_640441_004.Vertex328]
FEATURE [App::Link] _pinconnector_640441_005  label="3pinconnector-640441-006"
  LinkPlacement = pos=(33.0962,92.7862,1.778) rot=(0,1,0;3.14159rad)
  LinkedObject = -> Part__Feature011
  Placement = pos=(33.0962,92.7862,1.778) rot=(0,1,0;3.14159rad)
FEATURE [App::FeaturePython] Joint013  label="Fixed013"  # Assembly joint (typed FeaturePython)
  Activated = true
  AngleMax = 0
  AngleMin = 0
  Detach1 = false
  Detach2 = false
  Distance = 0
  Distance2 = 0
  EnableAngleMax = false
  EnableAngleMin = false
  EnableLengthMax = false
  EnableLengthMin = false
  JointType = 0 (Fixed)
  LengthMax = 0
  LengthMin = 0
  Offset1 = pos=(18.8722,44.9072,0) rot=(0,0,1;3.14159rad)
  Placement1 = pos=(32.2072,92.0242,1.778) rot=(0,0,1;3.14159rad)
  Placement2 = pos=(0.889,-0.762,0) rot=(0,0,1;0rad)
  Reference1 = -> Assembly [pcb_imported.Face5,pcb_imported.Edge49]
  Reference2 = -> Assembly [_pinconnector_640441_005.Face186,_pinconnector_640441_005.Vertex338]
FEATURE [Part::Feature] Part__Feature012  label="CUI_PJ-202A"
  shape: bbox 14.41 x 14.87 x 9.41 mm, 65 faces (baked)
FEATURE [App::Link] CUI_PJ_202A  label="CUI_PJ-202A001"
  LinkPlacement = pos=(-2.69501,66.04,8.278) rot=(0,0.707107,0.707107;3.14159rad)
  LinkedObject = -> Part__Feature012
  Placement = pos=(-2.69501,66.04,8.278) rot=(0,0.707107,0.707107;3.14159rad)
FEATURE [App::FeaturePython] Joint014  label="Fixed014"  # Assembly joint (typed FeaturePython)
  Activated = true
  AngleMax = 0
  AngleMin = 0
  Detach1 = false
  Detach2 = false
  Distance = 0
  Distance2 = 0
  EnableAngleMax = false
  EnableAngleMin = false
  EnableLengthMax = false
  EnableLengthMin = false
  JointType = 0 (Fixed)
  LengthMax = 0
  LengthMin = 0
  Offset1 = pos=(-15.24,40.64,0) rot=(0,0,-1;1.5708rad)
  Placement1 = pos=(4.318,66.04,1.778) rot=(0,0,-1;1.5708rad)
  Placement2 = pos=(-7.01301,-6.5,0) rot=(0.57735,0.57735,-0.57735;2.0944rad)
  Reference1 = -> Assembly [pcb_imported.Face5,pcb_imported.Vertex225]
  Reference2 = -> Assembly [CUI_PJ_202A.Face5,CUI_PJ_202A.Face5]
FEATURE [Part::Feature] Part__Feature013  label="SLW-864547-5A-RA-D"
  shape: bbox 8.6 x 9.5 x 7.5 mm, 89 faces (baked)
FEATURE [App::Link] SLW_864547_5A_RA_D  label="SLW-864547-5A-RA-D001"
  LinkPlacement = pos=(2.563,37.056,1.72323) rot=(0,0,1;4.71239rad)
  LinkedObject = -> Part__Feature013
  Placement = pos=(2.563,37.056,1.72323) rot=(0,0,1;4.71239rad)
FEATURE [App::FeaturePython] Joint015  label="Fixed015"  # Assembly joint (typed FeaturePython)
  Activated = true
  AngleMax = 0
  AngleMin = 0
  Detach1 = false
  Detach2 = false
  Distance = 0
  Distance2 = 0
  EnableAngleMax = false
  EnableAngleMin = false
  EnableLengthMax = false
  EnableLengthMin = false
  JointType = 0 (Fixed)
  LengthMax = 0
  LengthMin = 0
  Offset1 = pos=(13.716,26.416,0) rot=(0,0,1;1.5708rad)
  Placement1 = pos=(15.466,26.266,0.0547674) rot=(0,0,-1;4.71239rad)
  Placement2 = pos=(28.829,21.59,1.778) rot=(0,0,1;0rad)
  Reference1 = -> Assembly [SLW_864547_5A_RA_D.Face17,SLW_864547_5A_RA_D.Vertex24]
  Reference2 = -> Assembly [pcb_imported.Face5,pcb_imported.Edge60]
FEATURE [App::Link] SLW_864547_5A_RA_D001  label="SLW-864547-5A-RA-D002"
  LinkPlacement = pos=(2.563,49.756,1.72323) rot=(0,0,1;4.71239rad)
  LinkedObject = -> Part__Feature013
  Placement = pos=(2.563,49.756,1.72323) rot=(0,0,1;4.71239rad)
FEATURE [App::FeaturePython] Joint016  label="Fixed016"  # Assembly joint (typed FeaturePython)
  Activated = true
  AngleMax = 0
  AngleMin = 0
  Detach1 = false
  Detach2 = false
  Distance = 0
  Distance2 = 0
  EnableAngleMax = false
  EnableAngleMin = false
  EnableLengthMax = false
  EnableLengthMin = false
  JointType = 0 (Fixed)
  LengthMax = 0
  LengthMin = 0
  Offset1 = pos=(-12.7,0,0) rot=(0,0,1;0rad)
  Placement1 = pos=(-12.7,0,0) rot=(0,0,1;0rad)
  Reference1 = -> Assembly [SLW_864547_5A_RA_D.,SLW_864547_5A_RA_D.]
  Reference2 = -> Assembly [SLW_864547_5A_RA_D001.,SLW_864547_5A_RA_D001.]
FEATURE [Part::Feature] Part__Feature014  label="quiik"
  Placement = pos=(-3.68878,1.645,-3.606e-13) rot=(0,1,0;1.5708rad)
  shape: bbox 4.95 x 2.96 x 6 mm, 217 faces (baked)
FEATURE [Part::Feature] Part__Feature015  label="USB-C"
  Placement = pos=(-33.8738,-1.46186,-5.52737) rot=(0,-1,0;1.5708rad)
  shape: bbox 7.904 x 3.166 x 11.6 mm, 550 faces (baked)
FEATURE [Part::Feature] Part__Feature016  label="pcb-ft232"
  Placement = pos=(0.206219,-1.323e-13,11.43) rot=(0,0,1;0rad)
  shape: bbox 38.1 x 2 x 22.86 mm, 6 faces (baked)
FEATURE [App::Link] Ft232H_2_assembly001  label="Ft232H-2-assembly001"
  LinkPlacement = pos=(37.8726,15.185,11.684) rot=(1,0,0;1.5708rad)
  LinkedObject = -> Ft232H_2_assembly
  Placement = pos=(37.8726,15.185,11.684) rot=(1,0,0;1.5708rad)
FEATURE [App::FeaturePython] Joint017  label="Fixed017"  # Assembly joint (typed FeaturePython)
  Activated = true
  AngleMax = 0
  AngleMin = 0
  Detach1 = false
  Detach2 = false
  Distance = 0
  Distance2 = 0
  EnableAngleMax = false
  EnableAngleMin = false
  EnableLengthMax = false
  EnableLengthMin = false
  JointType = 0 (Fixed)
  LengthMax = 0
  LengthMin = 0
  Offset1 = pos=(-52.1462,11.176,-9.906) rot=(0,0,1;1.5708rad)
  Placement1 = pos=(-7.874,-9.906,-63.5762) rot=(1,0,0;4.71239rad)
  Placement2 = pos=(30.2048,67.3312,1.778) rot=(0,0,1;0rad)
  Reference1 = -> Assembly [Ft232H_2_assembly001.Part__Feature016.Face6,Ft232H_2_assembly001.Part__Feature016.Face6]
  Reference2 = -> Assembly [pcb_imported.Face5,pcb_imported.Vertex359]
FEATURE [Assembly::JointGroup] Joints
  Group = -> [GroundedJoint,Joint,Joint001,Joint002,Joint003,Joint004,Joint005,Joint008,Joint009,Joint010,Joint011,Joint012,Joint013,Joint014,Joint015,Joint016,Joint017]
FEATURE [Assembly::AssemblyObject] Assembly  label="PCB Assembly"
  Group = -> [Joints,pcb_imported,GroundedJoint,WP154A4SUREQBFZGC,Joint,WP154A4SUREQBFZGC001,Joint001,WP154A4SUREQBFZGC002,Joint002,WP154A4SUREQBFZGC003,Joint003,WP154A4SUREQBFZGC004,Joint004,WP154A4SUREQBFZGC005,Joint005,Dual_RCA,Joint008,Pro_Mini,Joint009,SPST_momentary001,Joint010,_pinconnector_640441_3,Joint011,_pinconnector_640441_004,Joint012,_pinconnector_640441_005,Joint013,CUI_PJ_202A,Joint014,+6 more]
  Origin = -> Origin001
  Type = Assembly
FEATURE [PartDesign::SubShapeBinder] Binder
  BindCopyOnChange = 0
  BindMode = 0
  ClaimChildren = false
  Context = -> Assembly [Ft232H_2_assembly001.Body001.Binder.]
  Fuse = false
  MakeFace = true
  OffsetFill = false
  OffsetIntersection = false
  OffsetJoinType = 0
  OffsetOpenResult = false
  PartialLoad = false
  Refine = true
  Relative = true
  Support = -> [Part__Feature016]
  _Version = 2
FEATURE [Sketcher::SketchObject] Sketch
  ArcFitTolerance = 1e-06
  AttachmentSupport = -> [Binder]
  ExternalGeometry = -> [Binder]
  FullyConstrained = true
  MakeInternals = false
  MapMode = 5
  Placement = pos=(0,-1.32e-13,0) rot=(1,0,0;1.5708rad)
  sketch-geometry (10):
    g0: LineSegment [constr] StartX=-31.5438 StartY=10.16 StartZ=0 EndX=-31.5438 EndY=-10.16 EndZ=0
    g1: LineSegment [constr] StartX=-31.5438 StartY=-10.16 StartZ=0 EndX=-6.14378 EndY=-10.16 EndZ=0
    g2: LineSegment [constr] StartX=-6.14378 StartY=-10.16 StartZ=0 EndX=-6.14378 EndY=10.16 EndZ=0
    g3: LineSegment [constr] StartX=-6.14378 StartY=10.16 StartZ=0 EndX=-31.5438 EndY=10.16 EndZ=0
    g4: GeomPoint [constr] X=-37.8938 Y=-3.968e-13 Z=0
    g5: GeomPoint [constr] X=-31.5438 Y=-3.968e-13 Z=0
    g6: GeomPoint [constr] X=-18.8438 Y=11.43 Z=0
    g7: GeomPoint [constr] X=-18.8438 Y=10.16 Z=0
    g8: Circle [constr] CenterX=-31.5438 CenterY=10.16 CenterZ=0 NormalX=0 NormalY=0 NormalZ=1 AngleXU=0 Radius=0.4445
    g9: Circle CenterX=-29.0038 CenterY=10.16 CenterZ=0 NormalX=0 NormalY=0 NormalZ=1 AngleXU=0 Radius=0.4445
  constraints (23):
    c: DistanceX(g-3,g-1) = 37.8938
    c: Distance(g-3,g-4) = 22.86
    c: Coincident(g1,g2)
    c: Coincident(g2,g3)
    c: Coincident(g3,g0)
    c: Vertical(g0)
    c: Vertical(g2)
    c: Horizontal(g1)
    c: Horizontal(g3)
    c: DistanceX(g3,g3) = 25.4
    c: DistanceY(g2,g2) = 20.32
    c: Symmetric(g-3,g-4,g4)
    c: Symmetric(g0,g0,g5)
    c: Horizontal(g5,g4)
    c: Symmetric(g2,g0,g7)
    c: Symmetric(g-3,g-3,g6)
    c: Vertical(g7,g6)
    c: Coincident(g8,g0)
    c: Diameter(g8) = 0.889
    c: Coincident(g1,g0)
    c: Horizontal(g0,g9)
    c: DistanceX(g0,g9) = 2.54
    c: Equal(g8,g9)
FEATURE [PartDesign::Pad] Pad
  Direction = (0,-1,2e-16)
  Length = 9.906
  Length2 = 10
  Profile = -> Sketch
  ReferenceAxis = -> Sketch [N_Axis]
  Refine = true
  Suppressed = false
  Type = 0
FEATURE [PartDesign::Body] Body001  label="Body"
  AllowCompound = false
  Group = -> [Binder,Sketch,Pad]
  Origin = -> Origin005
  Tip = -> Pad
FEATURE [App::Part] Ft232H_2_assembly  label="Ft232H-2-assembly"
  Group = -> [Part__Feature014,Part__Feature015,Part__Feature016,Body001]
  Origin = -> Origin004
